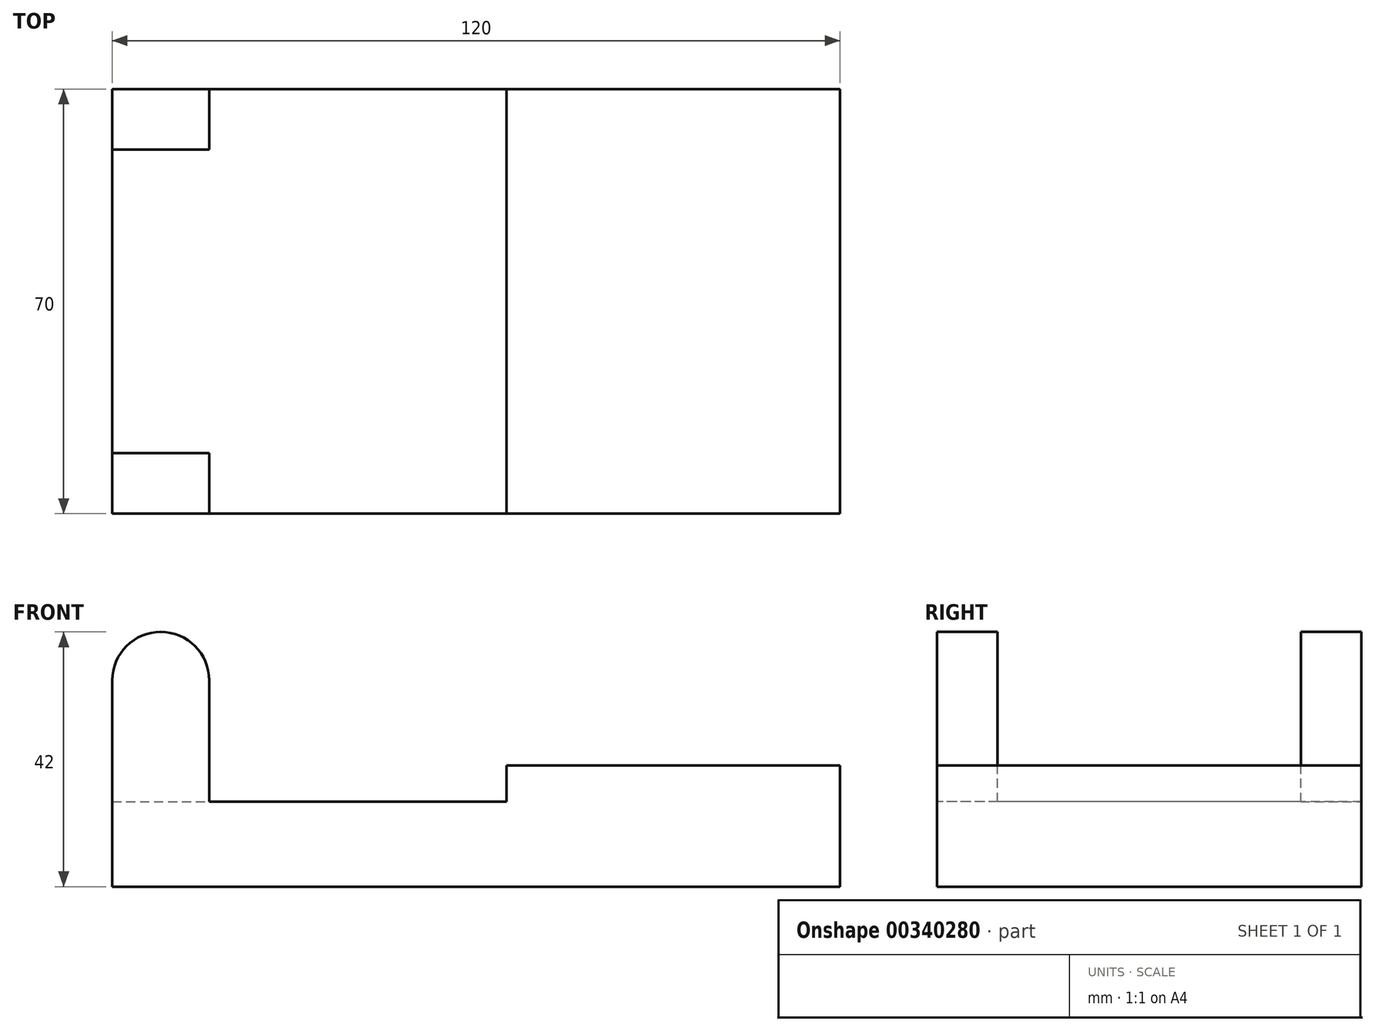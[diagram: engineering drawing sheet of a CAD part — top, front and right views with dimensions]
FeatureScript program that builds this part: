
annotation { "Feature Type Name" : "Feature", "Feature Type Description" : "" }
export const myFeature = defineFeature(function(context is Context, id is Id, definition is map)
    precondition{}
    {
        {
            var Q0;
            Q0=qCreatedBy(makeId("Top.planeOp"),FACE);
            var sketch = newSketch(context, id + "F0", { "sketchPlane" : qUnion([Q0])});
            skLineSegment(sketch, "E0.bottom", {"start": v(60, 35) * mm, "end": v(-60, 35) * mm});
            skLineSegment(sketch, "E0.top", {"start": v(60, -35) * mm, "end": v(-60, -35) * mm});
            skLineSegment(sketch, "E0.left", {"start": v(60, 35) * mm, "end": v(60, -35) * mm});
            skLineSegment(sketch, "E0.right", {"start": v(-60, 35) * mm, "end": v(-60, -35) * mm});
            skPoint(sketch, "E0.middle", {"position": v(0, 0) * mm});
            skSolve(sketch);
        }
        {
            var Q0;
            Q0=makeQuery(id+"F0.imprint","IMPRINT",FACE,{"disambiguationData":[TD([[makeQuery(id+"F0.imprint","IMPRINT",EDGE,{"derivedFrom":sQuery(id+"F0.wireOp",EDGE,"E0.bottom")}),1.0]])]});
            extrude(context, id + "F1", {"entities" : qUnion([Q0]), "depth" : 20 * mm});
        }
        {
            var Q0;
            Q0=makeQuery(id+"F1.opExtrude","SWEPT_FACE",FACE,{"disambiguationData":[OSD([sQuery(id+"F0.wireOp",EDGE,"E0.top")])]});
            var sketch = newSketch(context, id + "F2", { "sketchPlane" : qUnion([Q0])});
            skLineSegment(sketch, "E1.bottom", {"start": v(-60, 20) * mm, "end": v(5, 20) * mm});
            skLineSegment(sketch, "E1.top", {"start": v(-60, 14) * mm, "end": v(5, 14) * mm});
            skLineSegment(sketch, "E1.left", {"start": v(-60, 20) * mm, "end": v(-60, 14) * mm});
            skLineSegment(sketch, "E1.right", {"start": v(5, 20) * mm, "end": v(5, 14) * mm});
            skSolve(sketch);
        }
        {
            var Q0;
            Q0=makeQuery(id+"F2.imprint","IMPRINT",FACE,{"disambiguationData":[TD([[makeQuery(id+"F2.imprint","IMPRINT",EDGE,{"derivedFrom":sQuery(id+"F2.wireOp",EDGE,"E1.bottom")}),1.0]])]});
            extrude(context, id + "F3", {"entities" : qUnion([Q0]), "operationType" : NewBodyOperationType.REMOVE, "oppositeDirection" : true, "depth" : 100 * mm});
        }
        {
            var Q0;
            Q0=makeQuery(id+"F1.opExtrude","SWEPT_FACE",FACE,{"disambiguationData":[OSD([sQuery(id+"F0.wireOp",EDGE,"E0.top")])]});
            var sketch = newSketch(context, id + "F4", { "sketchPlane" : qUnion([Q0])});
            skLineSegment(sketch, "E2.bottom", {"start": v(-60, 14) * mm, "end": v(-44, 14) * mm});
            skLineSegment(sketch, "E2.top", {"start": v(-60, 34) * mm, "end": v(-44, 34) * mm});
            skLineSegment(sketch, "E2.left", {"start": v(-60, 14) * mm, "end": v(-60, 34) * mm});
            skLineSegment(sketch, "E2.right", {"start": v(-44, 14) * mm, "end": v(-44, 34) * mm});
            skCircle(sketch, "E3", {"center": v(-52, 34) * mm, "radius": 8 * mm});
            skSolve(sketch);
        }
        {
            var Q0;
            {var subQ0=sQuery(id+"F4.wireOp",EDGE,"E2.top");Q0=makeQuery(id+"F4.imprint","IMPRINT",FACE,{"disambiguationData":[TD([[makeQuery(id+"F4.imprint","IMPRINT",EDGE,{"derivedFrom":subQ0}),1.0]])]});}
            var Q1;
            {var subQ0=sQuery(id+"F4.wireOp",EDGE,"E2.top");Q1=makeQuery(id+"F4.imprint","IMPRINT",FACE,{"disambiguationData":[TD([[makeQuery(id+"F4.imprint","IMPRINT",EDGE,{"derivedFrom":subQ0}),-1.0]])]});}
            var Q2;
            Q2=makeQuery(id+"F4.imprint","IMPRINT",FACE,{"disambiguationData":[TD([[makeQuery(id+"F4.imprint","IMPRINT",EDGE,{"derivedFrom":sQuery(id+"F4.wireOp",EDGE,"E2.bottom")}),1.0]])]});
            extrude(context, id + "F5", {"entities" : qUnion([Q0, Q1, Q2]), "operationType" : NewBodyOperationType.ADD, "oppositeDirection" : true, "depth" : 10 * mm});
        }
        {
            var Q0;
            Q0=makeQuery(id+"F1.opExtrude","SWEPT_FACE",FACE,{"disambiguationData":[OSD([sQuery(id+"F0.wireOp",EDGE,"E0.bottom")])]});
            var sketch = newSketch(context, id + "F6", { "sketchPlane" : qUnion([Q0])});
            skLineSegment(sketch, "E4.bottom", {"start": v(60, 14) * mm, "end": v(44, 14) * mm});
            skLineSegment(sketch, "E4.top", {"start": v(60, 34) * mm, "end": v(44, 34) * mm});
            skLineSegment(sketch, "E4.left", {"start": v(60, 14) * mm, "end": v(60, 34) * mm});
            skLineSegment(sketch, "E4.right", {"start": v(44, 14) * mm, "end": v(44, 34) * mm});
            skCircle(sketch, "E5", {"center": v(52, 34) * mm, "radius": 8 * mm});
            skSolve(sketch);
        }
        {
            var Q0;
            Q0 = qSketchRegion(id + "F6", true);
            var Q1;
            {var subQ0=sQuery(id+"F6.wireOp",EDGE,"E4.top");Q1=makeQuery(id+"F6.imprint","IMPRINT",FACE,{"disambiguationData":[TD([[makeQuery(id+"F6.imprint","IMPRINT",EDGE,{"derivedFrom":subQ0}),-1.0]])]});}
            extrude(context, id + "F7", {"entities" : qUnion([Q0, Q1]), "operationType" : NewBodyOperationType.ADD, "oppositeDirection" : true, "depth" : 10 * mm});
        }
    });
